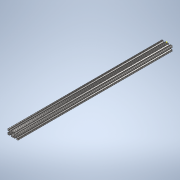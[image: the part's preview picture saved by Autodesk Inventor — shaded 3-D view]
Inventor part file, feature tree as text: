
AUTODESK INVENTOR PART (.ipt)
format: ipt  version: 2020 (Build 240168000, 168)  size: 365,568 bytes
history: native  units: in
note: dims shown in document units (in); Inventor stores cm internally (conversion verified against a paired STEP export)
features: sketch x2, extrude x1
ambient origin geometry x8: Origin, YZ Plane, XZ Plane, XY Plane, X Axis, Y Axis, Z Axis, Center Point
bodies: Solid1 (feature_tree)
feature tree (3):
  extrude  "Extrusion1"  [1 undecoded]
  sketch  "Sketch2"
  sketch  "Sketch1"  dims[d0=29.0in d1=0.0in]
note: 1 required parameter value undecoded (feature->parameter linkage not recoverable at this tier; creation-order binding heuristic only, values carry confidence <= 0.55)
